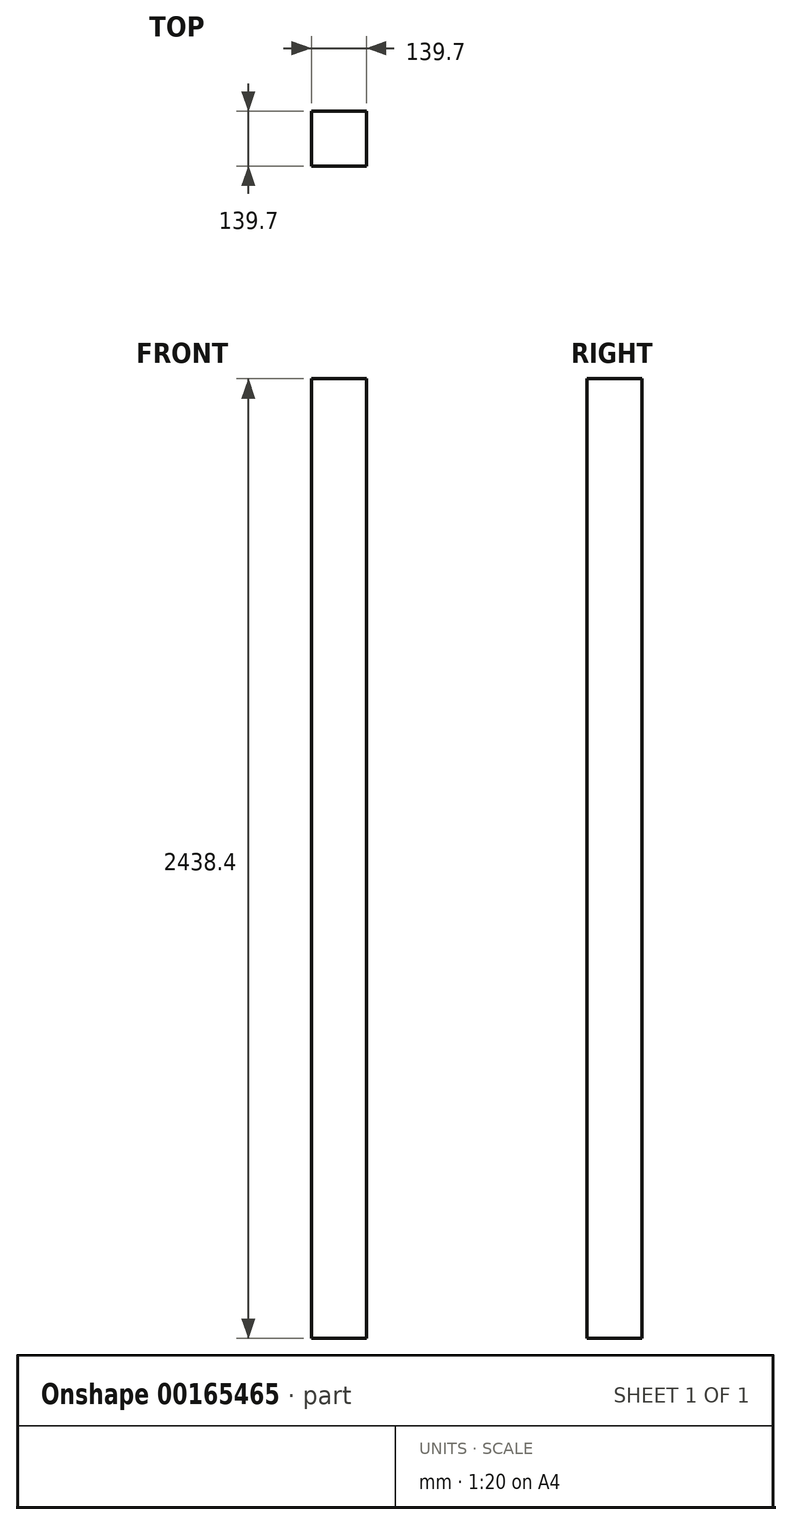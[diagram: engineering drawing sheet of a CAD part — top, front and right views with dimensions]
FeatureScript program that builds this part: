
annotation { "Feature Type Name" : "Feature", "Feature Type Description" : "" }
export const myFeature = defineFeature(function(context is Context, id is Id, definition is map)
    precondition{}
    {
        {
            var Q0;
            Q0=qCreatedBy(makeId("Top.planeOp"),FACE);
            var sketch = newSketch(context, id + "F0", { "sketchPlane" : qUnion([Q0])});
            skLineSegment(sketch, "E0.bottom", {"start": v(69.85, 69.85) * mm, "end": v(-69.85, 69.85) * mm});
            skLineSegment(sketch, "E0.top", {"start": v(69.85, -69.85) * mm, "end": v(-69.85, -69.85) * mm});
            skLineSegment(sketch, "E0.left", {"start": v(69.85, 69.85) * mm, "end": v(69.85, -69.85) * mm});
            skLineSegment(sketch, "E0.right", {"start": v(-69.85, 69.85) * mm, "end": v(-69.85, -69.85) * mm});
            skPoint(sketch, "E0.middle", {"position": v(0, 0) * mm});
            skSolve(sketch);
        }
        {
            var Q0;
            Q0 = qSketchRegion(id + "F0", true);
            extrude(context, id + "F1", {"entities" : qUnion([Q0]), "depth" : 2438.4 * mm});
        }
    });
